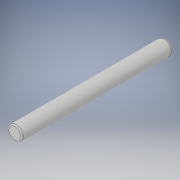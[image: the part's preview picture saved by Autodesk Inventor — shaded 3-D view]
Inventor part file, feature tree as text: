
AUTODESK INVENTOR PART (.ipt)
format: ipt  version: 2019 (Build 230136000, 136)  size: 100,864 bytes
history: native  units: mm
features: extrude x1, fillet x1, sketch x1
ambient origin geometry x8: Origin, YZ Plane, XZ Plane, XY Plane, X Axis, Y Axis, Z Axis, Center Point
bodies: Solid1 (feature_tree)
feature tree (3):
  extrude  "Extrusion1"  Depth=12.0mm TaperAngle=0.0deg
  fillet  "Fillet1"  Radius=0.1mm
  sketch  "Sketch1"  dims[d0=1.15mm d1=12.0mm d2=0.0mm d3=0.1mm]
